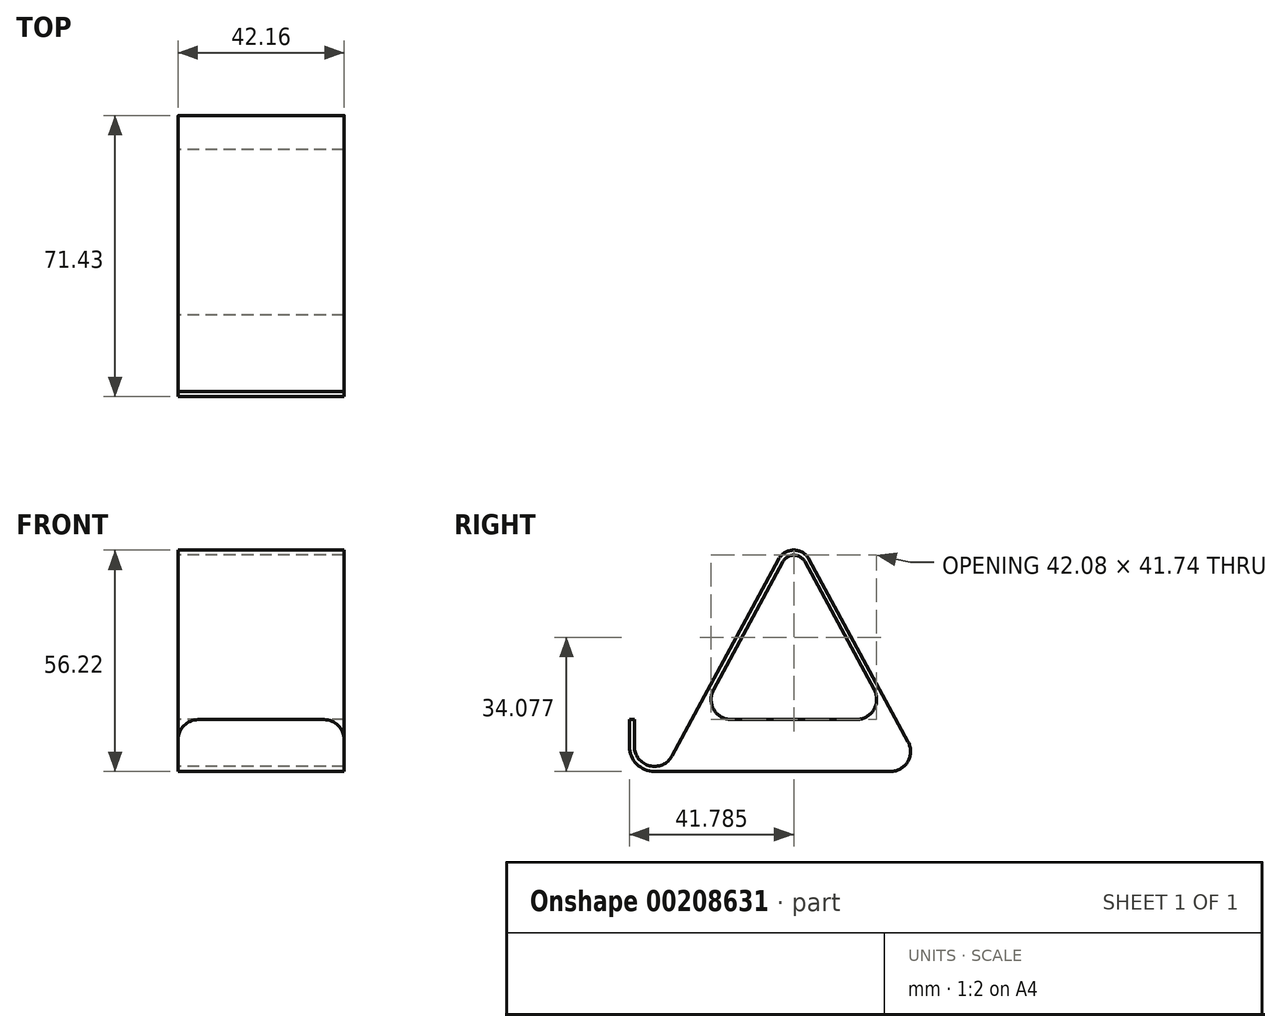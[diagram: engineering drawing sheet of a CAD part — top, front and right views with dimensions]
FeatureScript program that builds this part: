
annotation { "Feature Type Name" : "Feature", "Feature Type Description" : "" }
export const myFeature = defineFeature(function(context is Context, id is Id, definition is map)
    precondition{}
    {
        {
            var Q0;
            Q0=qCreatedBy(makeId("Right.planeOp"),FACE);
            var sketch = newSketch(context, id + "F0", { "sketchPlane" : qUnion([Q0])});
            skArc(sketch, "E0", {"start": v(-6.35, 0) * mm, "mid": v(-4.5, -4.5) * mm, "end": v(0, -6.35) * mm});
            skArc(sketch, "E1", {"start": v(38.2, 46.95) * mm, "mid": v(35.44, 48.6) * mm, "end": v(32.68, 46.95) * mm});
            skLineSegment(sketch, "E2", {"start": v(32.68, 46.95) * mm, "end": v(15, 14.36) * mm});
            skLineSegment(sketch, "E3", {"start": v(35.44, 45.46) * mm, "end": v(35.44, -11.01) * mm, "construction": true});
            skLineSegment(sketch, "E4.MirrorCS", {"start": v(38.2, 46.95) * mm, "end": v(55.86, 14.36) * mm});
            skLineSegment(sketch, "E5", {"start": v(0, -6.35) * mm, "end": v(60, -6.35) * mm, "construction": true});
            skPoint(sketch, "E6.orphan", {"position": v(65.29, -3.03) * mm});
            skLineSegment(sketch, "E7", {"start": v(-6.35, 0) * mm, "end": v(-6.35, 6.8) * mm});
            skLineSegment(sketch, "E8.0", {"start": v(-5.08, 0) * mm, "end": v(-5.08, 6.8) * mm});
            skLineSegment(sketch, "E8.1", {"start": v(39.3, 47.56) * mm, "end": v(64.47, 1.15) * mm});
            skArc(sketch, "E8.2", {"start": v(39.3, 47.56) * mm, "mid": v(35.44, 49.87) * mm, "end": v(31.56, 47.56) * mm});
            skLineSegment(sketch, "E8.3", {"start": v(31.56, 47.56) * mm, "end": v(4.47, -2.42) * mm});
            skArc(sketch, "E8.4", {"start": v(-5.08, 0) * mm, "mid": v(-1.25, -4.92) * mm, "end": v(4.47, -2.42) * mm});
            skLineSegment(sketch, "E9", {"start": v(-6.35, 6.8) * mm, "end": v(-5.08, 6.8) * mm});
            skLineSegment(sketch, "E10", {"start": v(0, -6.35) * mm, "end": v(68.53, -6.35) * mm});
            skLineSegment(sketch, "E11.0", {"start": v(19.47, 6.86) * mm, "end": v(51.4, 6.86) * mm});
            skPoint(sketch, "E12.orphan", {"position": v(5.58, -3.03) * mm});
            skPoint(sketch, "E13.visualSharp", {"position": v(10.94, 6.86) * mm});
            skArc(sketch, "E13.filletArc", {"start": v(15, 14.36) * mm, "mid": v(15.1, 9.34) * mm, "end": v(19.47, 6.86) * mm});
            skPoint(sketch, "E14.visualSharp", {"position": v(59.93, 6.86) * mm});
            skArc(sketch, "E14.filletArc", {"start": v(51.4, 6.86) * mm, "mid": v(55.76, 9.34) * mm, "end": v(55.86, 14.36) * mm});
            skArc(sketch, "E15.filletArc", {"start": v(60, -6.35) * mm, "mid": v(64.37, -3.87) * mm, "end": v(64.47, 1.15) * mm});
            skSolve(sketch);
        }
        {
            var Q0;
            {var subQ0=sQuery(id+"F0.wireOp",EDGE,"E0");Q0=makeQuery(id+"F0.imprint","IMPRINT",FACE,{"disambiguationData":[TD([[makeQuery(id+"F0.imprint","IMPRINT",EDGE,{"derivedFrom":subQ0}),1.0]])]});}
            extrude(context, id + "F1", {"entities" : qUnion([Q0]), "depth" : 42.16 * mm});
        }
        {
            var Q0;
            Q0=makeQuery(id+"F1.opExtrude","CAP_EDGE",EDGE,{"disambiguationData":[OSD([sQuery(id+"F0.wireOp",EDGE,"E9")])],"isStart":false});
            var Q1;
            Q1=makeQuery(id+"F1.opExtrude","CAP_EDGE",EDGE,{"disambiguationData":[OSD([sQuery(id+"F0.wireOp",EDGE,"E9")])],"isStart":true});
            fillet(context, id + "F2", {"entities" : qUnion([Q0, Q1]), "radius" : 5.08 * mm, "tangentPropagation" : true, "allowEdgeOverflow" : false});
        }
    });
